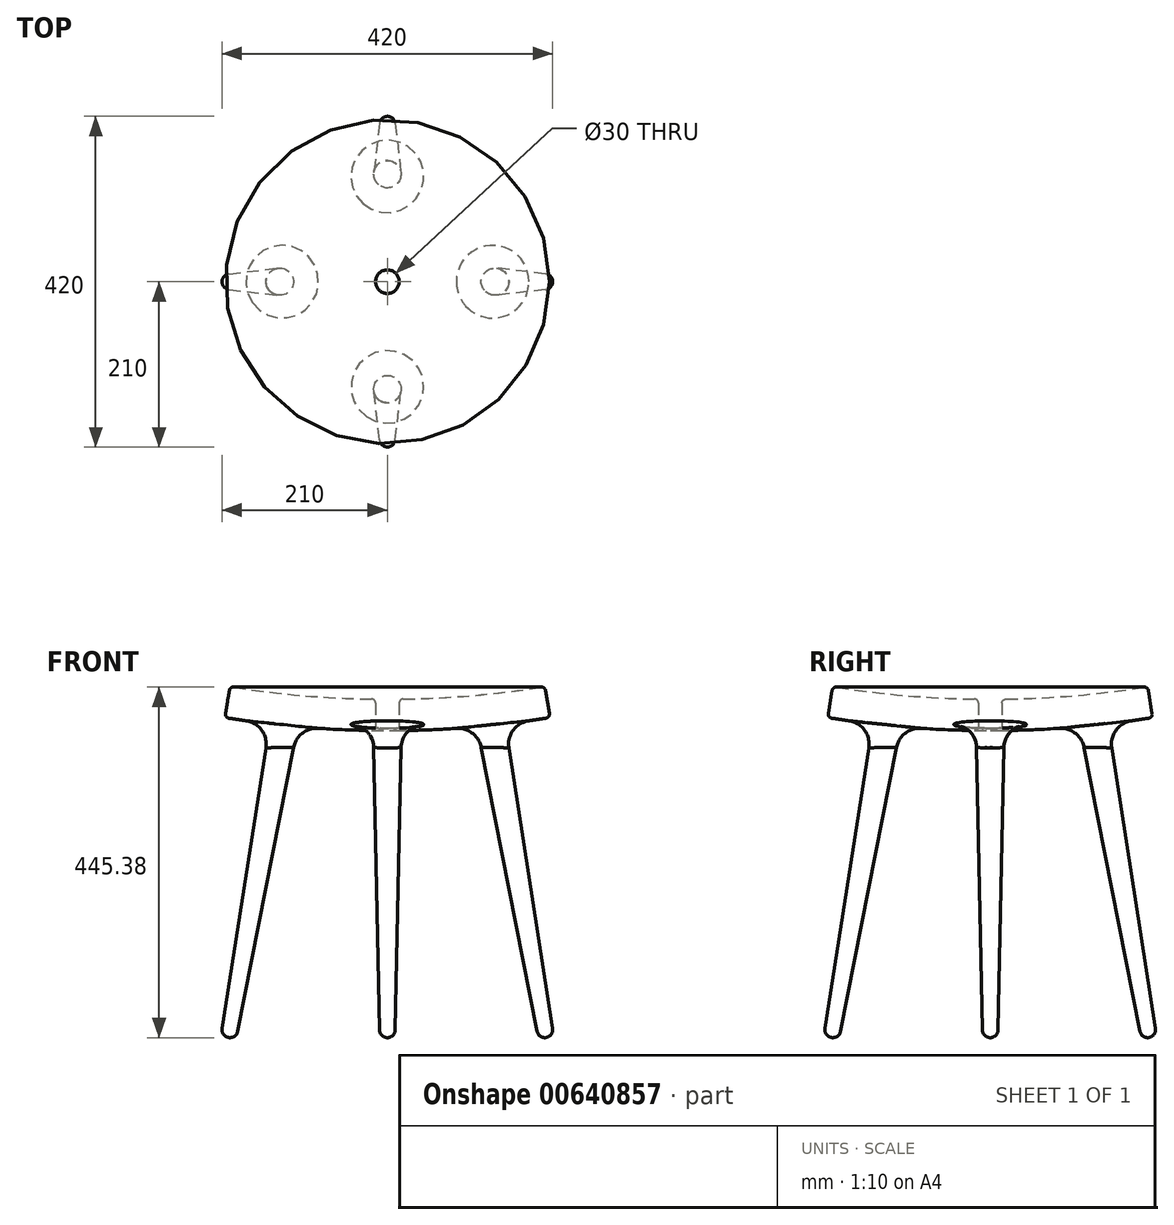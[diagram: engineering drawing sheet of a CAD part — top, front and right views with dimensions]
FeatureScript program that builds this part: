
annotation { "Feature Type Name" : "Feature", "Feature Type Description" : "" }
export const myFeature = defineFeature(function(context is Context, id is Id, definition is map)
    precondition{}
    {
        {
            var Q0;
            Q0=qCreatedBy(makeId("Front.planeOp"),FACE);
            var sketch = newSketch(context, id + "F0", { "sketchPlane" : qUnion([Q0])});
            skArc(sketch, "E0", {"start": v(0, 430) * mm, "mid": v(100.32, 434.03) * mm, "end": v(200, 446.1) * mm});
            skLineSegment(sketch, "E1", {"start": v(0, 1680) * mm, "end": v(0, 0) * mm, "construction": true});
            skLineSegment(sketch, "E2", {"start": v(200, 446.1) * mm, "end": v(206.4, 406.62) * mm});
            skArc(sketch, "E3.0", {"start": v(0, 390) * mm, "mid": v(103.53, 394.16) * mm, "end": v(206.4, 406.62) * mm});
            skLineSegment(sketch, "E4", {"start": v(0, 430) * mm, "end": v(0, 390) * mm});
            skSolve(sketch);
        }
        {
            var Q0;
            Q0=makeQuery(id+"F0.imprint","IMPRINT",FACE,{"disambiguationData":[TD([[makeQuery(id+"F0.imprint","IMPRINT",EDGE,{"derivedFrom":sQuery(id+"F0.wireOp",EDGE,"E0")}),-1.0]])]});
            var Q1;
            Q1=sQuery(id+"F0.wireOp",EDGE,"E4");
            revolve(context, id + "F1", {"entities" : qUnion([Q0]), "axis" : qUnion([Q1]), "revolveType" : RevolveType.FULL});
        }
        {
            var Q0;
            Q0=qCreatedBy(makeId("Front.planeOp"),FACE);
            var sketch = newSketch(context, id + "F2", { "sketchPlane" : qUnion([Q0])});
            skLineSegment(sketch, "E5", {"start": v(0, 0) * mm, "end": v(-292.35, 0) * mm, "construction": true});
            skArc(sketch, "E6", {"start": v(-201.74, 0.15) * mm, "mid": v(-194.35, 1.75) * mm, "end": v(-190.19, 8.07) * mm});
            skLineSegment(sketch, "E7", {"start": v(-201.74, 0.15) * mm, "end": v(-130.54, 403.92) * mm});
            skLineSegment(sketch, "E8", {"start": v(-130.54, 403.92) * mm, "end": v(-112.81, 400.8) * mm});
            skLineSegment(sketch, "E9", {"start": v(-112.81, 400.8) * mm, "end": v(-190.19, 8.07) * mm});
            skSolve(sketch);
        }
        {
            var Q0;
            Q0 = qSketchRegion(id + "F2", true);
            var Q1;
            Q1 = qSketchRegion(id + "F4", true);
            var Q2;
            Q2=sQuery(id+"F2.wireOp",EDGE,"E7");
            revolve(context, id + "F3", {"entities" : qUnion([Q0, Q1]), "axis" : qUnion([Q2]), "revolveType" : RevolveType.FULL});
        }
        {
            var Q0;
            Q0=qCreatedBy(makeId("Front.planeOp"),FACE);
            var sketch = newSketch(context, id + "F4", { "sketchPlane" : qUnion([Q0])});
            skLineSegment(sketch, "E10", {"start": v(0, 0) * mm, "end": v(0, 248.92) * mm, "construction": true});
            skSolve(sketch);
        }
        {
            var Q0;
            Q0=makeQuery(id+"F3.opRevolve","SWEPT_BODY",BODY,{"disambiguationData":[OSD([sQuery(id+"F2.wireOp",EDGE,"E6"),sQuery(id+"F2.wireOp",EDGE,"E7"),sQuery(id+"F2.wireOp",EDGE,"E8"),sQuery(id+"F2.wireOp",EDGE,"E9")])]});
            var Q1;
            Q1=sQuery(id+"F4.wireOp",EDGE,"E10");
            circularPattern(context, id + "F5", {"entities" : qUnion([Q0]), "axis" : qUnion([Q1]), "angle" : 360 * degree, "instanceCount" : 4, "equalSpace" : true});
        }
        {
            var Q0;
            Q0=makeQuery(id+"F1.opRevolve","SWEPT_BODY",BODY,{"disambiguationData":[OSD([sQuery(id+"F0.wireOp",EDGE,"E0"),sQuery(id+"F0.wireOp",EDGE,"E2"),sQuery(id+"F0.wireOp",EDGE,"E3.0"),sQuery(id+"F0.wireOp",EDGE,"E4")])]});
            var Q1;
            Q1=makeQuery(id+"F5.opPattern","COPY",BODY,{"derivedFrom":makeQuery(id+"F3.opRevolve","SWEPT_BODY",BODY,{"disambiguationData":[OSD([sQuery(id+"F2.wireOp",EDGE,"E6"),sQuery(id+"F2.wireOp",EDGE,"E7"),sQuery(id+"F2.wireOp",EDGE,"E8"),sQuery(id+"F2.wireOp",EDGE,"E9")])]}),"instanceName":"2"});
            var Q2;
            Q2=makeQuery(id+"F5.opPattern","COPY",BODY,{"derivedFrom":makeQuery(id+"F3.opRevolve","SWEPT_BODY",BODY,{"disambiguationData":[OSD([sQuery(id+"F2.wireOp",EDGE,"E6"),sQuery(id+"F2.wireOp",EDGE,"E7"),sQuery(id+"F2.wireOp",EDGE,"E8"),sQuery(id+"F2.wireOp",EDGE,"E9")])]}),"instanceName":"1"});
            var Q3;
            Q3=makeQuery(id+"F5.opPattern","COPY",BODY,{"derivedFrom":makeQuery(id+"F3.opRevolve","SWEPT_BODY",BODY,{"disambiguationData":[OSD([sQuery(id+"F2.wireOp",EDGE,"E6"),sQuery(id+"F2.wireOp",EDGE,"E7"),sQuery(id+"F2.wireOp",EDGE,"E8"),sQuery(id+"F2.wireOp",EDGE,"E9")])]}),"instanceName":"3"});
            var Q4;
            Q4=makeQuery(id+"F3.opRevolve","SWEPT_BODY",BODY,{"disambiguationData":[OSD([sQuery(id+"F2.wireOp",EDGE,"E6"),sQuery(id+"F2.wireOp",EDGE,"E7"),sQuery(id+"F2.wireOp",EDGE,"E8"),sQuery(id+"F2.wireOp",EDGE,"E9")])]});
            booleanBodies(context, id + "F6", {"operationType" : BooleanOperationType.UNION, "tools" : qUnion([Q0, Q1, Q2, Q3, Q4])});
        }
        {
            var Q0;
            Q0=makeQuery(id+"F6.opBoolean","INTERSECT",EDGE,{"derivedFrom":[makeQuery(id+"F1.opRevolve","SWEPT_FACE",FACE,{"disambiguationData":[OSD([sQuery(id+"F0.wireOp",EDGE,"E3.0")])]}),makeQuery(id+"F3.opRevolve","SWEPT_FACE",FACE,{"disambiguationData":[OSD([sQuery(id+"F2.wireOp",EDGE,"E9")])]})]});
            var Q1;
            Q1=makeQuery(id+"F6.opBoolean","INTERSECT",EDGE,{"derivedFrom":[makeQuery(id+"F1.opRevolve","SWEPT_FACE",FACE,{"disambiguationData":[OSD([sQuery(id+"F0.wireOp",EDGE,"E3.0")])]}),makeQuery(id+"F5.opPattern","COPY",FACE,{"derivedFrom":makeQuery(id+"F3.opRevolve","SWEPT_FACE",FACE,{"disambiguationData":[OSD([sQuery(id+"F2.wireOp",EDGE,"E9")])]}),"instanceName":"1"})]});
            var Q2;
            Q2=makeQuery(id+"F6.opBoolean","INTERSECT",EDGE,{"derivedFrom":[makeQuery(id+"F1.opRevolve","SWEPT_FACE",FACE,{"disambiguationData":[OSD([sQuery(id+"F0.wireOp",EDGE,"E3.0")])]}),makeQuery(id+"F5.opPattern","COPY",FACE,{"derivedFrom":makeQuery(id+"F3.opRevolve","SWEPT_FACE",FACE,{"disambiguationData":[OSD([sQuery(id+"F2.wireOp",EDGE,"E9")])]}),"instanceName":"2"})]});
            var Q3;
            Q3=makeQuery(id+"F6.opBoolean","INTERSECT",EDGE,{"derivedFrom":[makeQuery(id+"F1.opRevolve","SWEPT_FACE",FACE,{"disambiguationData":[OSD([sQuery(id+"F0.wireOp",EDGE,"E3.0")])]}),makeQuery(id+"F5.opPattern","COPY",FACE,{"derivedFrom":makeQuery(id+"F3.opRevolve","SWEPT_FACE",FACE,{"disambiguationData":[OSD([sQuery(id+"F2.wireOp",EDGE,"E9")])]}),"instanceName":"3"})]});
            fillet(context, id + "F7", {"entities" : qUnion([Q0, Q1, Q2, Q3]), "radius" : 30 * mm, "tangentPropagation" : true, "allowEdgeOverflow" : false});
        }
        {
            var Q0;
            Q0=makeQuery(id+"F1.opRevolve","SWEPT_EDGE",EDGE,{"disambiguationData":[OSD([sQuery(id+"F0.wireOp",EDGE,"E0"),sQuery(id+"F0.wireOp",EDGE,"E2")])]});
            var Q1;
            Q1=makeQuery(id+"F1.opRevolve","SWEPT_EDGE",EDGE,{"disambiguationData":[OSD([sQuery(id+"F0.wireOp",EDGE,"E2"),sQuery(id+"F0.wireOp",EDGE,"E3.0")])]});
            fillet(context, id + "F8", {"entities" : qUnion([Q0, Q1]), "radius" : 5 * mm, "tangentPropagation" : true, "allowEdgeOverflow" : false});
        }
        {
            var Q0;
            Q0=qCreatedBy(makeId("Top.planeOp"),FACE);
            var sketch = newSketch(context, id + "F9", { "sketchPlane" : qUnion([Q0])});
            skCircle(sketch, "E11", {"center": v(0, 0) * mm, "radius": 15 * mm});
            skSolve(sketch);
        }
        {
            var Q0;
            Q0 = qSketchRegion(id + "F9", true);
            extrude(context, id + "F10", {"entities" : qUnion([Q0]), "operationType" : NewBodyOperationType.REMOVE, "depth" : 819 * mm, "offsetDistance" : 25 * mm});
        }
        {
            var Q0;
            Q0=makeQuery(id+"F10.boolean.opBoolean","INTERSECT",EDGE,{"derivedFrom":[makeQuery(id+"F1.opRevolve","SWEPT_FACE",FACE,{"disambiguationData":[OSD([sQuery(id+"F0.wireOp",EDGE,"E0")])]}),makeQuery(id+"F10.opExtrude","SWEPT_FACE",FACE,{"disambiguationData":[OSD([sQuery(id+"F9.wireOp",EDGE,"E11")])]})]});
            var Q1;
            Q1=makeQuery(id+"F10.boolean.opBoolean","INTERSECT",EDGE,{"derivedFrom":[makeQuery(id+"F1.opRevolve","SWEPT_FACE",FACE,{"disambiguationData":[OSD([sQuery(id+"F0.wireOp",EDGE,"E3.0")])]}),makeQuery(id+"F10.opExtrude","SWEPT_FACE",FACE,{"disambiguationData":[OSD([sQuery(id+"F9.wireOp",EDGE,"E11")])]})]});
            fillet(context, id + "F11", {"entities" : qUnion([Q0, Q1]), "radius" : 5 * mm, "tangentPropagation" : true, "allowEdgeOverflow" : false});
        }
    });
